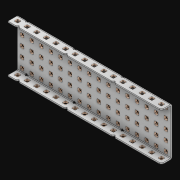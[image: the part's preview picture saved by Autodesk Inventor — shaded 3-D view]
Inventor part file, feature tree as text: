
AUTODESK INVENTOR PART (.ipt)
format: ipt  version: 2021 (Build 250183000, 183)  size: 3,261,952 bytes
history: native  units: in
note: dims shown in document units (in); Inventor stores cm internally (conversion verified against a paired STEP export)
features: extrude x113, other x112, sketch x4, thicken_offset x3, pattern_linear x3, imported_body x1
ambient origin geometry x8: Origin, YZ Plane, XZ Plane, XY Plane, X Axis, Y Axis, Z Axis, Center Point
bodies: Solid1 (feature_tree)
feature tree (236):
  thicken_offset  "Thicken1"
  thicken_offset  "Thicken2"
  thicken_offset  "Thicken3"
  pattern_linear  "Rectangular Pattern1"  Spacing1=0.001in  [1 undecoded]
  pattern_linear  "Rectangular Pattern2"  Spacing1=0.001in  [1 undecoded]
  pattern_linear  "Rectangular Pattern3"  Spacing1=0.182in  [1 undecoded]
  extrude  "Extrusion1"  Depth=0.063in TaperAngle=0.0deg
  sketch  "Sketch1"  dims[d0=0.001in]
  other  "Srf1"
  sketch  "Sketch2"  dims[d1=0.001in]
  other  "Srf2"
  sketch  "Sketch3"  dims[d2=0.001in]
  other  "Srf3"
  other  "Srf4"
  other  "Srf5"
  other  "Srf6"
  other  "Srf7"
  other  "Srf8"
  other  "Srf9"
  other  "Srf10"
  other  "Srf11"
  other  "Srf12"
  other  "Srf13"
  other  "Srf14"
  other  "Srf15"
  other  "Srf16"
  other  "Srf17"
  other  "Srf18"
  other  "Srf38"
  other  "Srf39"
  other  "Srf40"
  other  "Srf41"
  other  "Srf42"
  other  "Srf43"
  other  "Srf44"
  other  "Srf45"
  other  "Srf46"
  other  "Srf47"
  other  "Srf48"
  other  "Srf49"
  other  "Srf50"
  other  "Srf51"
  other  "Srf52"
  other  "Srf72"
  other  "Srf73"
  other  "Srf74"
  other  "Srf75"
  other  "Srf76"
  other  "Srf77"
  other  "Srf78"
  other  "Srf79"
  other  "Srf80"
  other  "Srf81"
  other  "Srf82"
  other  "Srf83"
  other  "Srf84"
  other  "Srf85"
  other  "Srf86"
  other  "Srf106"
  other  "Srf107"
  other  "Srf108"
  other  "Srf109"
  other  "Srf110"
  other  "Srf111"
  other  "Srf112"
  other  "Srf113"
  other  "Srf114"
  other  "Srf115"
  other  "Srf116"
  other  "Srf117"
  other  "Srf118"
  other  "Srf119"
  other  "Srf120"
  other  "Srf121"
  other  "Srf141"
  other  "Srf142"
  other  "Srf143"
  other  "Srf144"
  other  "Srf145"
  other  "Srf146"
  other  "Srf147"
  other  "Srf148"
  other  "Srf149"
  other  "Srf150"
  other  "Srf151"
  other  "Srf152"
  other  "Srf153"
  other  "Srf154"
  other  "Srf155"
  other  "Srf156"
  other  "Srf176"
  other  "Srf177"
  other  "Srf178"
  other  "Srf179"
  other  "Srf180"
  other  "Srf181"
  other  "Srf182"
  other  "Srf183"
  other  "Srf184"
  other  "Srf185"
  other  "Srf186"
  other  "Srf187"
  other  "Srf188"
  other  "Srf189"
  other  "Srf190"
  other  "Srf191"
  other  "Srf211"
  other  "Srf212"
  other  "Srf213"
  other  "Srf214"
  other  "Srf215"
  other  "Srf216"
  other  "Srf217"
  other  "Srf218"
  other  "Srf219"
  other  "Srf220"
  other  "Srf221"
  other  "Srf222"
  other  "Srf223"
  other  "Srf224"
  other  "Srf225"
  other  "Srf226"
  sketch  "Sketch4"  dims[d3=0.001in d4=0.001in d5=0.001in d6=0.182in d7=0.063in d8=0.0in d9=0.182in d10=0.063in d11=0.0in d12=0.182in d13=0.063in d14=0.0in d17=0.5in d18=6.2992in d20=0.5in d21=6.2992in d23=0.5in d24=1.9685in d26=0.5in d27=9.5in d28=0.0in]
  imported_body  "Imported1"
  extrude  "ExtrusionSrf1"  Depth=0.063in
  extrude  "ExtrusionSrf2"  Depth=0.063in TaperAngle=0.0deg
  extrude  "ExtrusionSrf3"  Depth=0.063in
  extrude  "ExtrusionSrf4"  Depth=0.063in TaperAngle=0.0deg
  extrude  "ExtrusionSrf5"  Depth=0.063in
  extrude  "ExtrusionSrf6"  Depth=0.063in
  extrude  "ExtrusionSrf7"  Depth=0.063in
  extrude  "ExtrusionSrf8"  Depth=0.063in
  extrude  "ExtrusionSrf9"  Depth=0.063in
  extrude  "ExtrusionSrf10"  Depth=0.063in
  extrude  "ExtrusionSrf11"  Depth=0.063in
  extrude  "ExtrusionSrf12"  TaperAngle=0.0deg  [1 undecoded]
  extrude  "ExtrusionSrf13"  [1 undecoded]
  extrude  "ExtrusionSrf14"  [1 undecoded]
  extrude  "ExtrusionSrf15"  [1 undecoded]
  extrude  "ExtrusionSrf16"  [1 undecoded]
  extrude  "ExtrusionSrf17"  [1 undecoded]
  extrude  "ExtrusionSrf18"  [1 undecoded]
  extrude  "ExtrusionSrf38"  [1 undecoded]
  extrude  "ExtrusionSrf39"  [1 undecoded]
  extrude  "ExtrusionSrf40"  [1 undecoded]
  extrude  "ExtrusionSrf41"  [1 undecoded]
  extrude  "ExtrusionSrf42"  [1 undecoded]
  extrude  "ExtrusionSrf43"  [1 undecoded]
  extrude  "ExtrusionSrf44"  [1 undecoded]
  extrude  "ExtrusionSrf45"  [1 undecoded]
  extrude  "ExtrusionSrf46"  [1 undecoded]
  extrude  "ExtrusionSrf47"  [1 undecoded]
  extrude  "ExtrusionSrf48"  [1 undecoded]
  extrude  "ExtrusionSrf49"  [1 undecoded]
  extrude  "ExtrusionSrf50"  [1 undecoded]
  extrude  "ExtrusionSrf51"  [1 undecoded]
  extrude  "ExtrusionSrf52"  [1 undecoded]
  extrude  "ExtrusionSrf72"  [1 undecoded]
  extrude  "ExtrusionSrf73"  [1 undecoded]
  extrude  "ExtrusionSrf74"  [1 undecoded]
  extrude  "ExtrusionSrf75"  [1 undecoded]
  extrude  "ExtrusionSrf76"  [1 undecoded]
  extrude  "ExtrusionSrf77"  [1 undecoded]
  extrude  "ExtrusionSrf78"  [1 undecoded]
  extrude  "ExtrusionSrf79"  [1 undecoded]
  extrude  "ExtrusionSrf80"  [1 undecoded]
  extrude  "ExtrusionSrf81"  [1 undecoded]
  extrude  "ExtrusionSrf82"  [1 undecoded]
  extrude  "ExtrusionSrf83"  [1 undecoded]
  extrude  "ExtrusionSrf84"  [1 undecoded]
  extrude  "ExtrusionSrf85"  [1 undecoded]
  extrude  "ExtrusionSrf86"  [1 undecoded]
  extrude  "ExtrusionSrf106"  [1 undecoded]
  extrude  "ExtrusionSrf107"  [1 undecoded]
  extrude  "ExtrusionSrf108"  [1 undecoded]
  extrude  "ExtrusionSrf109"  [1 undecoded]
  extrude  "ExtrusionSrf110"  [1 undecoded]
  extrude  "ExtrusionSrf111"  [1 undecoded]
  extrude  "ExtrusionSrf112"  [1 undecoded]
  extrude  "ExtrusionSrf113"  [1 undecoded]
  extrude  "ExtrusionSrf114"  [1 undecoded]
  extrude  "ExtrusionSrf115"  [1 undecoded]
  extrude  "ExtrusionSrf116"  [1 undecoded]
  extrude  "ExtrusionSrf117"  [1 undecoded]
  extrude  "ExtrusionSrf118"  [1 undecoded]
  extrude  "ExtrusionSrf119"  [1 undecoded]
  extrude  "ExtrusionSrf120"  [1 undecoded]
  extrude  "ExtrusionSrf121"  [1 undecoded]
  extrude  "ExtrusionSrf141"  [1 undecoded]
  extrude  "ExtrusionSrf142"  [1 undecoded]
  extrude  "ExtrusionSrf143"  [1 undecoded]
  extrude  "ExtrusionSrf144"  [1 undecoded]
  extrude  "ExtrusionSrf145"  [1 undecoded]
  extrude  "ExtrusionSrf146"  [1 undecoded]
  extrude  "ExtrusionSrf147"  [1 undecoded]
  extrude  "ExtrusionSrf148"  [1 undecoded]
  extrude  "ExtrusionSrf149"  [1 undecoded]
  extrude  "ExtrusionSrf150"  [1 undecoded]
  extrude  "ExtrusionSrf151"  [1 undecoded]
  extrude  "ExtrusionSrf152"  [1 undecoded]
  extrude  "ExtrusionSrf153"  [1 undecoded]
  extrude  "ExtrusionSrf154"  [1 undecoded]
  extrude  "ExtrusionSrf155"  [1 undecoded]
  extrude  "ExtrusionSrf156"  [1 undecoded]
  extrude  "ExtrusionSrf176"  [1 undecoded]
  extrude  "ExtrusionSrf177"  [1 undecoded]
  extrude  "ExtrusionSrf178"  [1 undecoded]
  extrude  "ExtrusionSrf179"  [1 undecoded]
  extrude  "ExtrusionSrf180"  [1 undecoded]
  extrude  "ExtrusionSrf181"  [1 undecoded]
  extrude  "ExtrusionSrf182"  [1 undecoded]
  extrude  "ExtrusionSrf183"  [1 undecoded]
  extrude  "ExtrusionSrf184"  [1 undecoded]
  extrude  "ExtrusionSrf185"  [1 undecoded]
  extrude  "ExtrusionSrf186"  [1 undecoded]
  extrude  "ExtrusionSrf187"  [1 undecoded]
  extrude  "ExtrusionSrf188"  [1 undecoded]
  extrude  "ExtrusionSrf189"  [1 undecoded]
  extrude  "ExtrusionSrf190"  [1 undecoded]
  extrude  "ExtrusionSrf191"  [1 undecoded]
  extrude  "ExtrusionSrf211"  [1 undecoded]
  extrude  "ExtrusionSrf212"  [1 undecoded]
  extrude  "ExtrusionSrf213"  [1 undecoded]
  extrude  "ExtrusionSrf214"  [1 undecoded]
  extrude  "ExtrusionSrf215"  [1 undecoded]
  extrude  "ExtrusionSrf216"  [1 undecoded]
  extrude  "ExtrusionSrf217"  [1 undecoded]
  extrude  "ExtrusionSrf218"  [1 undecoded]
  extrude  "ExtrusionSrf219"  [1 undecoded]
  extrude  "ExtrusionSrf220"  [1 undecoded]
  extrude  "ExtrusionSrf221"  [1 undecoded]
  extrude  "ExtrusionSrf222"  [1 undecoded]
  extrude  "ExtrusionSrf223"  [1 undecoded]
  extrude  "ExtrusionSrf224"  [1 undecoded]
  extrude  "ExtrusionSrf225"  [1 undecoded]
  extrude  "ExtrusionSrf226"  [1 undecoded]
note: 104 required parameter values undecoded (feature->parameter linkage not recoverable at this tier; creation-order binding heuristic only, values carry confidence <= 0.55)
